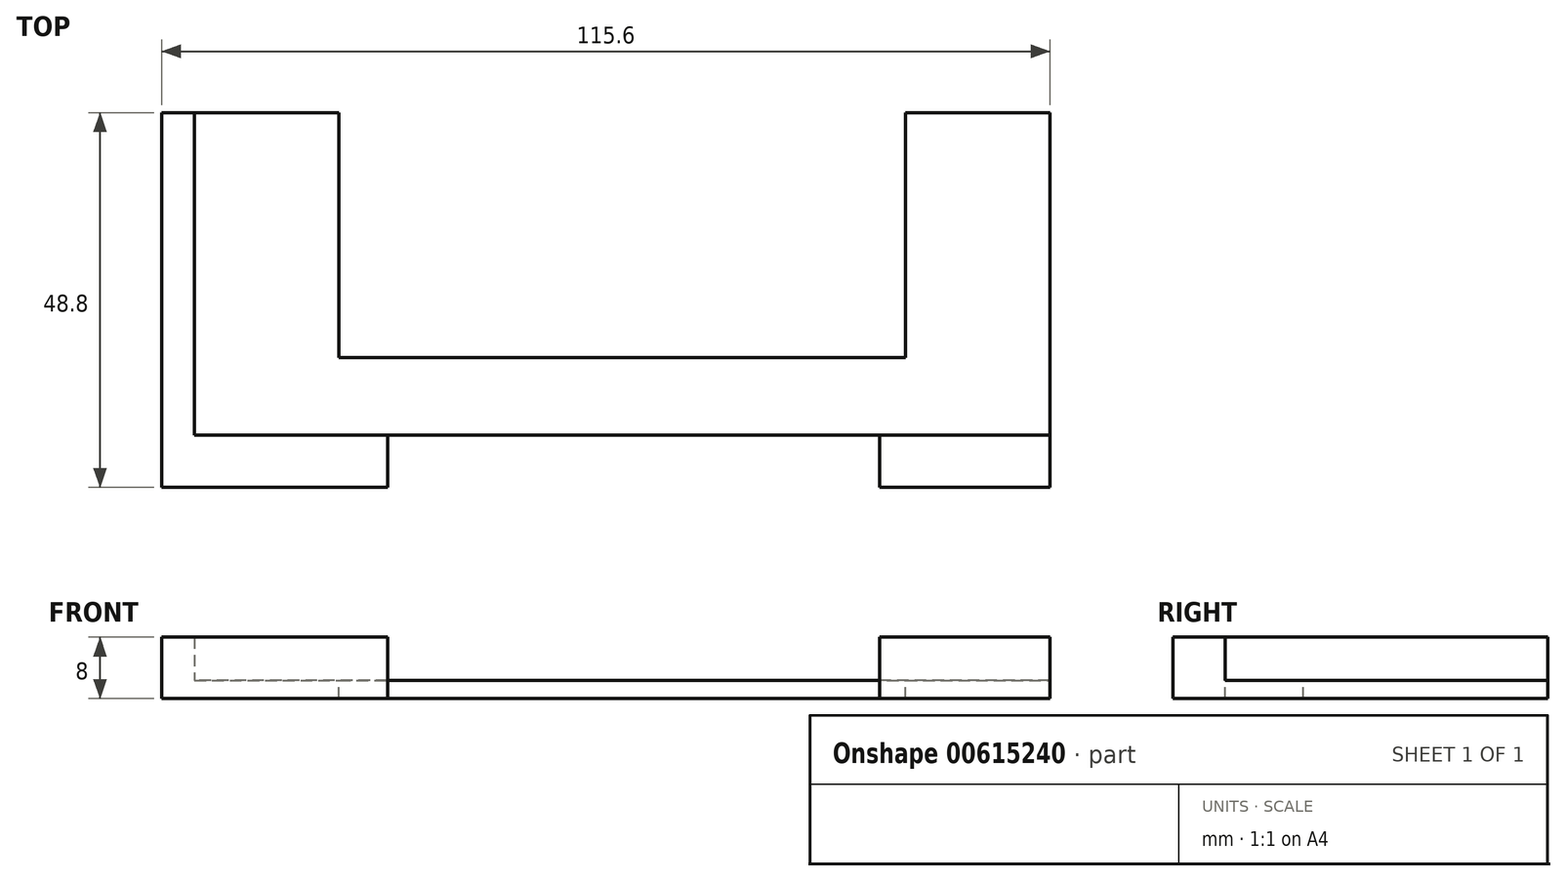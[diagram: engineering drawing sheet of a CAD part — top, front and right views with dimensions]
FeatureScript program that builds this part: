
annotation { "Feature Type Name" : "Feature", "Feature Type Description" : "" }
export const myFeature = defineFeature(function(context is Context, id is Id, definition is map)
    precondition{}
    {
        {
            var Q0;
            Q0=qCreatedBy(makeId("Top.planeOp"),FACE);
            var sketch = newSketch(context, id + "F0", { "sketchPlane" : qUnion([Q0])});
            skPoint(sketch, "E0.middle", {"position": v(0, 0) * mm});
            skLineSegment(sketch, "E1", {"start": v(-53.5, 24.5) * mm, "end": v(-53.5, -17.5) * mm});
            skLineSegment(sketch, "E2", {"start": v(-58, -17.5) * mm, "end": v(-57.8, -17.5) * mm});
            skLineSegment(sketch, "E3.0", {"start": v(-57.8, 24.5) * mm, "end": v(-57.8, -24.5) * mm});
            skLineSegment(sketch, "E4.0", {"start": v(58, -24.3) * mm, "end": v(-58, -24.3) * mm});
            skLineSegment(sketch, "E5.0", {"start": v(57.8, 24.5) * mm, "end": v(57.8, -24.5) * mm});
            skLineSegment(sketch, "E6", {"start": v(-57.8, 24.5) * mm, "end": v(-53.5, 24.5) * mm});
            skLineSegment(sketch, "E7", {"start": v(-53.5, 24.5) * mm, "end": v(53.1, 24.5) * mm});
            skLineSegment(sketch, "E8", {"start": v(53.1, 24.5) * mm, "end": v(57.8, 24.5) * mm});
            skLineSegment(sketch, "E9", {"start": v(58, -17.5) * mm, "end": v(57.8, -17.5) * mm});
            skLineSegment(sketch, "E10", {"start": v(-57.8, -17.5) * mm, "end": v(-58, -17.5) * mm});
            skLineSegment(sketch, "E11", {"start": v(57.8, -24.3) * mm, "end": v(58, -24.3) * mm});
            skLineSegment(sketch, "E12.trimOffspring", {"start": v(-53.5, -24.3) * mm, "end": v(-53.5, -24.5) * mm});
            skLineSegment(sketch, "E13.trimOffspring", {"start": v(53.1, -24.3) * mm, "end": v(53.1, -24.5) * mm});
            skLineSegment(sketch, "E14.trimOffspring", {"start": v(57.8, -17.5) * mm, "end": v(58, -17.5) * mm});
            skLineSegment(sketch, "E15", {"start": v(-53.5, -17.5) * mm, "end": v(53.1, -17.5) * mm});
            skLineSegment(sketch, "E16", {"start": v(53.1, -17.5) * mm, "end": v(58, -17.5) * mm});
            skSolve(sketch);
        }
        {
            var Q0;
            Q0=makeQuery(id+"F0.imprint","IMPRINT",FACE,{"disambiguationData":[TD([[makeQuery(id+"F0.imprint","IMPRINT",EDGE,{"derivedFrom":sQuery(id+"F0.wireOp",EDGE,"E1")}),-1.0]])]});
            var Q1;
            Q1=makeQuery(id+"F0.imprint","IMPRINT",FACE,{"disambiguationData":[TD([[makeQuery(id+"F0.imprint","IMPRINT",EDGE,{"derivedFrom":sQuery(id+"F0.wireOp",EDGE,"E1")}),1.0]])]});
            extrude(context, id + "F1", {"entities" : qUnion([Q0, Q1]), "depth" : 2.4 * mm, "offsetDistance" : 25 * mm});
        }
        {
            var Q0;
            Q0=makeQuery(id+"F0.imprint","IMPRINT",FACE,{"disambiguationData":[TD([[makeQuery(id+"F0.imprint","IMPRINT",EDGE,{"derivedFrom":sQuery(id+"F0.wireOp",EDGE,"E1")}),-1.0]])]});
            extrude(context, id + "F2", {"entities" : qUnion([Q0]), "operationType" : NewBodyOperationType.ADD, "depth" : 8 * mm, "offsetDistance" : 25 * mm});
        }
        {
            var Q0;
            Q0=makeQuery(id+"F2.opExtrude","CAP_FACE",FACE,{"disambiguationData":[OSD([sQuery(id+"F0.wireOp",EDGE,"E1"),sQuery(id+"F0.wireOp",EDGE,"E3.0"),sQuery(id+"F0.wireOp",EDGE,"E4.0"),sQuery(id+"F0.wireOp",EDGE,"E5.0"),sQuery(id+"F0.wireOp",EDGE,"E6"),sQuery(id+"F0.wireOp",EDGE,"E15"),sQuery(id+"F0.wireOp",EDGE,"E16")])],"isStart":false});
            var sketch = newSketch(context, id + "F3", { "sketchPlane" : qUnion([Q0])});
            skLineSegment(sketch, "E17", {"start": v(-28.36, -17.5) * mm, "end": v(-28.36, -24.3) * mm});
            skLineSegment(sketch, "E18", {"start": v(35.64, -17.5) * mm, "end": v(35.64, -24.3) * mm});
            skSolve(sketch);
        }
        {
            var Q0;
            {var subQ0=sQuery(id+"F3.wireOp",EDGE,"E17");Q0=makeQuery(id+"F3.imprint","IMPRINT",FACE,{"disambiguationData":[TD([[makeQuery(id+"F3.imprint","IMPRINT",EDGE,{"derivedFrom":subQ0}),1.0]])]});}
            extrude(context, id + "F4", {"entities" : qUnion([Q0]), "operationType" : NewBodyOperationType.REMOVE, "oppositeDirection" : true, "depth" : 25 * mm, "offsetDistance" : 25 * mm});
        }
        {
            var Q0;
            Q0=makeQuery(id+"F1.opExtrude","CAP_FACE",FACE,{"disambiguationData":[OSD([sQuery(id+"F0.wireOp",EDGE,"E3.0"),sQuery(id+"F0.wireOp",EDGE,"E4.0"),sQuery(id+"F0.wireOp",EDGE,"E5.0"),sQuery(id+"F0.wireOp",EDGE,"E6"),sQuery(id+"F0.wireOp",EDGE,"E7"),sQuery(id+"F0.wireOp",EDGE,"E8")])],"isStart":false});
            var sketch = newSketch(context, id + "F5", { "sketchPlane" : qUnion([Q0])});
            skLineSegment(sketch, "E19.0", {"start": v(39, 24.5) * mm, "end": v(39, -24.5) * mm});
            skLineSegment(sketch, "E20.0", {"start": v(-34.7, 24.5) * mm, "end": v(-34.7, -17.5) * mm});
            skLineSegment(sketch, "E21", {"start": v(-34.7, -7.37) * mm, "end": v(39, -7.37) * mm});
            skSolve(sketch);
        }
        {
            var Q0;
            {var subQ3=sQuery(id+"F5.wireOp",EDGE,"E21");Q0=makeQuery(id+"F5.imprint","IMPRINT",FACE,{"disambiguationData":[TD([[makeQuery(id+"F5.imprint","IMPRINT",EDGE,{"derivedFrom":subQ3}),1.0]])]});}
            extrude(context, id + "F6", {"entities" : qUnion([Q0]), "operationType" : NewBodyOperationType.REMOVE, "oppositeDirection" : true, "depth" : 25 * mm, "offsetDistance" : 25 * mm});
        }
    });
